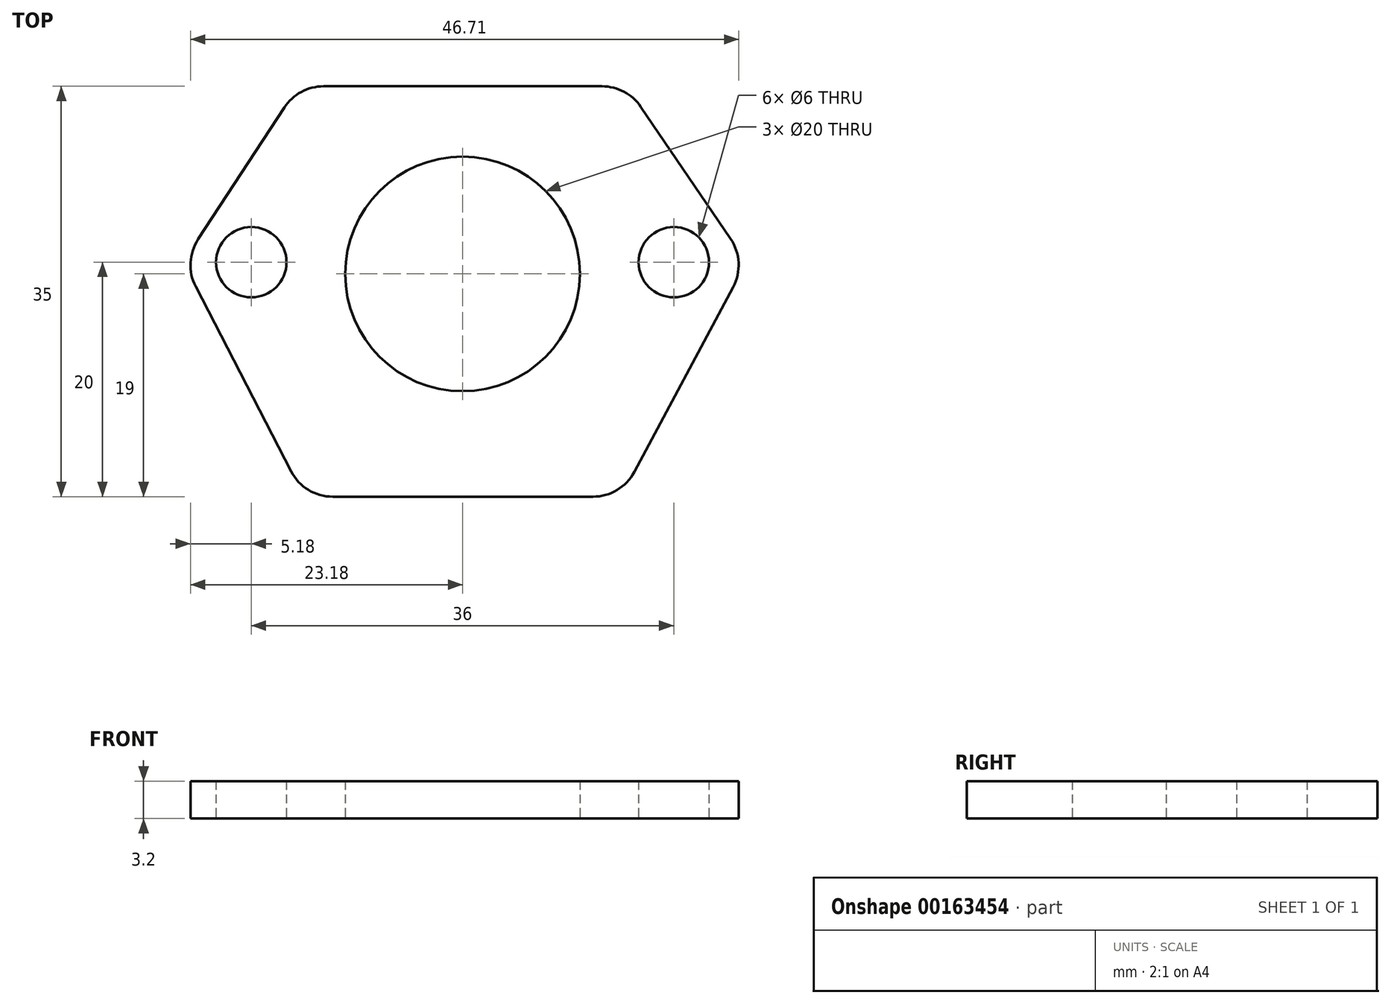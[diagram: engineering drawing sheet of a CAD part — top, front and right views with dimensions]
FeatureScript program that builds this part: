
annotation { "Feature Type Name" : "Feature", "Feature Type Description" : "" }
export const myFeature = defineFeature(function(context is Context, id is Id, definition is map)
    precondition{}
    {
        {
            var Q0;
            Q0=qCreatedBy(makeId("Top.planeOp"),FACE);
            var sketch = newSketch(context, id + "F0", { "sketchPlane" : qUnion([Q0])});
            skCircle(sketch, "E0", {"center": v(0, 0) * mm, "radius": 10 * mm});
            skLineSegment(sketch, "E1.bottom", {"start": v(-13.5, -19) * mm, "end": v(13.5, -19) * mm});
            skLineSegment(sketch, "E1.top", {"start": v(-14, 16) * mm, "end": v(14, 16) * mm});
            skCircle(sketch, "E2", {"center": v(18, 1) * mm, "radius": 3 * mm});
            skCircle(sketch, "E3", {"center": v(-18, 1) * mm, "radius": 3 * mm});
            skLineSegment(sketch, "E4", {"start": v(-18, 1) * mm, "end": v(18, 1) * mm, "construction": true});
            skLineSegment(sketch, "E5", {"start": v(24.2, 1) * mm, "end": v(13.5, -19) * mm});
            skLineSegment(sketch, "E6", {"start": v(-23.8, 1) * mm, "end": v(-13.5, -19) * mm});
            skLineSegment(sketch, "E7", {"start": v(-23.8, 1) * mm, "end": v(-14, 16) * mm});
            skLineSegment(sketch, "E8", {"start": v(24.2, 1) * mm, "end": v(14, 16) * mm});
            skPoint(sketch, "E9", {"position": v(0, 16) * mm});
            skPoint(sketch, "E10", {"position": v(0, -19) * mm});
            skPoint(sketch, "E11", {"position": v(0, 1) * mm});
            skLineSegment(sketch, "E12", {"start": v(0, 28.38) * mm, "end": v(0, -26.38) * mm, "construction": true});
            skSolve(sketch);
        }
        {
            var Q0;
            Q0 = qSketchRegion(id + "F0", true);
            extrude(context, id + "F1", {"entities" : qUnion([Q0]), "depth" : 3.2 * mm});
        }
        {
            var Q0;
            Q0=makeQuery(id+"F1.opExtrude","SWEPT_EDGE",EDGE,{"disambiguationData":[OSD([sQuery(id+"F0.wireOp",EDGE,"E1.bottom"),sQuery(id+"F0.wireOp",EDGE,"E6")])]});
            var Q1;
            Q1=makeQuery(id+"F1.opExtrude","SWEPT_EDGE",EDGE,{"disambiguationData":[OSD([sQuery(id+"F0.wireOp",EDGE,"E6"),sQuery(id+"F0.wireOp",EDGE,"E7")])]});
            var Q2;
            Q2=makeQuery(id+"F1.opExtrude","SWEPT_EDGE",EDGE,{"disambiguationData":[OSD([sQuery(id+"F0.wireOp",EDGE,"E1.bottom"),sQuery(id+"F0.wireOp",EDGE,"E5")])]});
            var Q3;
            Q3=makeQuery(id+"F1.opExtrude","SWEPT_EDGE",EDGE,{"disambiguationData":[OSD([sQuery(id+"F0.wireOp",EDGE,"E5"),sQuery(id+"F0.wireOp",EDGE,"E8")])]});
            var Q4;
            Q4=makeQuery(id+"F1.opExtrude","SWEPT_EDGE",EDGE,{"disambiguationData":[OSD([sQuery(id+"F0.wireOp",EDGE,"E1.top"),sQuery(id+"F0.wireOp",EDGE,"E8")])]});
            var Q5;
            Q5=makeQuery(id+"F1.opExtrude","SWEPT_EDGE",EDGE,{"disambiguationData":[OSD([sQuery(id+"F0.wireOp",EDGE,"E1.top"),sQuery(id+"F0.wireOp",EDGE,"E7")])]});
            fillet(context, id + "F2", {"entities" : qUnion([Q0, Q1, Q2, Q3, Q4, Q5]), "radius" : 4 * mm, "tangentPropagation" : true, "allowEdgeOverflow" : false});
        }
    });
